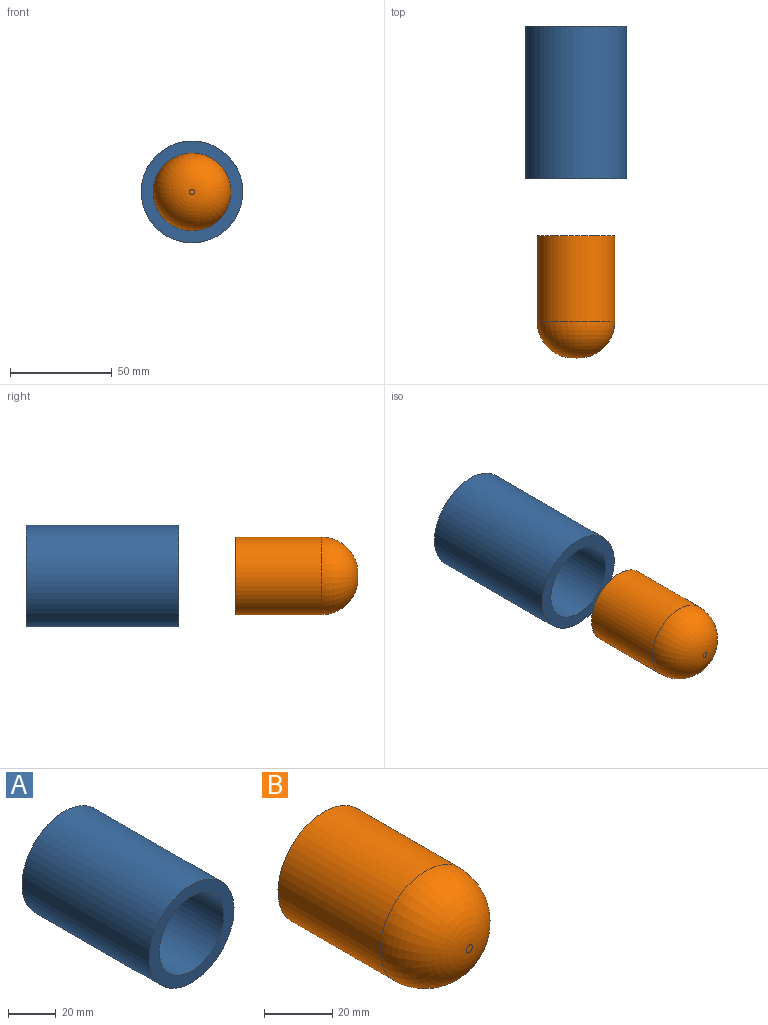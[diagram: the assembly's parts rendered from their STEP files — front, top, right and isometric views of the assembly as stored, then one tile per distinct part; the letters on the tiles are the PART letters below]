
ASSEMBLY  parts=2 mates=1
PART A: 4 faces, bbox 50x75x50 mm
  f0: cylinder r=25mm len=75mm, axis (0,1,0), area 11781mm2, adj f1,f2
  f1: plane 50x50mm, normal (0,-1,0), area 823.4mm2, adj f0,f3
  f2: plane 50x50mm, normal (0,1,0), area 823.4mm2, adj f0,f3
  f3: cylinder r=19.05mm len=75mm, axis (0,-1,0), area 8977.1mm2, adj f1,f2
PART B: 4 faces, bbox 38.1x60x38.1 mm
  f0: cylinder r=19.05mm len=42.22mm, axis (0,1,0), area 5053.5mm2, adj f2,f3
  f1: plane 2.54x2.54mm, normal (0,-1,0), area 5.1mm2, adj f3
  f2: plane 38.1x38.1mm, normal (0,1,0), area 1140.1mm2, adj f0
  f3: torus R=1.27mm, axis (0,-1,0), area 2209.2mm2, adj f0,f1
PLACE A t=(-2.87,123.87,-47.3)mm fixed
PLACE B rot(axis=(0,-1,0),31.4deg) t=(-2.87,28.14,-47.3)mm
MATE cylindrical A.f3 <-> B.f0  axis (0,-1,0) through (-2.87,86.37,-47.3)mm
